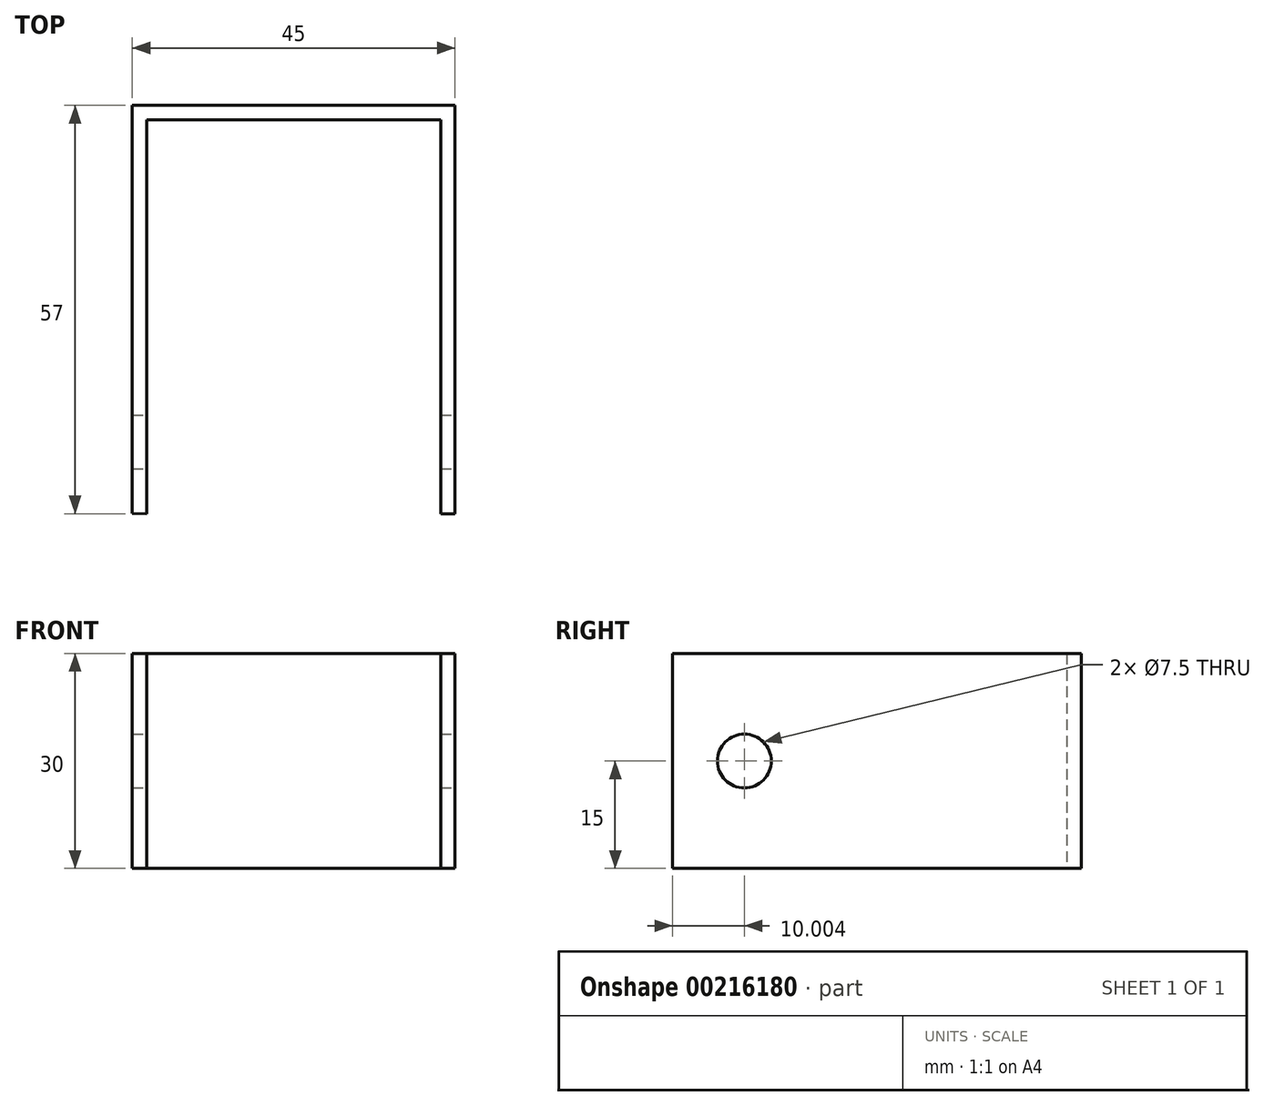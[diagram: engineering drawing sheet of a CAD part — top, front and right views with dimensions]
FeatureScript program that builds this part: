
annotation { "Feature Type Name" : "Feature", "Feature Type Description" : "" }
export const myFeature = defineFeature(function(context is Context, id is Id, definition is map)
    precondition{}
    {
        {
            var Q0;
            Q0=qCreatedBy(makeId("Top.planeOp"),FACE);
            var sketch = newSketch(context, id + "F0", { "sketchPlane" : qUnion([Q0])});
            skLineSegment(sketch, "E0", {"start": v(-24.23, 21.28) * mm, "end": v(16.77, 21.28) * mm});
            skLineSegment(sketch, "E1", {"start": v(-24.23, 21.28) * mm, "end": v(-24.23, -33.72) * mm});
            skLineSegment(sketch, "E2", {"start": v(16.77, 21.28) * mm, "end": v(16.77, -33.72) * mm});
            skLineSegment(sketch, "E3.0", {"start": v(-26.23, 23.28) * mm, "end": v(-26.23, -33.68) * mm});
            skLineSegment(sketch, "E3.1", {"start": v(-26.23, 23.28) * mm, "end": v(18.77, 23.28) * mm});
            skLineSegment(sketch, "E3.2", {"start": v(18.77, 23.28) * mm, "end": v(18.77, -33.72) * mm});
            skLineSegment(sketch, "E4", {"start": v(16.77, -33.72) * mm, "end": v(18.77, -33.72) * mm});
            skLineSegment(sketch, "E5", {"start": v(-24.23, -33.72) * mm, "end": v(-26.23, -33.68) * mm});
            skSolve(sketch);
        }
        {
            var Q0;
            Q0 = qSketchRegion(id + "F0", true);
            extrude(context, id + "F1", {"entities" : qUnion([Q0]), "depth" : 30 * mm});
        }
        {
            var Q0;
            Q0=makeQuery(id+"F1.opExtrude","SWEPT_FACE",FACE,{"disambiguationData":[OSD([sQuery(id+"F0.wireOp",EDGE,"E3.2")])]});
            var sketch = newSketch(context, id + "F2", { "sketchPlane" : qUnion([Q0])});
            skPoint(sketch, "E6", {"position": v(-23.72, 15) * mm});
            skPoint(sketch, "E7", {"position": v(-33.72, 15) * mm});
            skSolve(sketch);
        }
        {
            var Q0;
            Q0=sQuery(id+"F2.wireOp",VERTEX,"E6");
            var Q1;
            Q1=makeQuery(id+"F1.opExtrude","SWEPT_BODY",BODY,{"disambiguationData":[OSD([sQuery(id+"F0.wireOp",EDGE,"E0"),sQuery(id+"F0.wireOp",EDGE,"E1"),sQuery(id+"F0.wireOp",EDGE,"E2"),sQuery(id+"F0.wireOp",EDGE,"E3.0"),sQuery(id+"F0.wireOp",EDGE,"E3.1"),sQuery(id+"F0.wireOp",EDGE,"E3.2"),sQuery(id+"F0.wireOp",EDGE,"E4"),sQuery(id+"F0.wireOp",EDGE,"E5")])]});
            hole(context, id + "F3", {"style" : HoleStyle.SIMPLE, "endStyle" : HoleEndStyle.THROUGH, "holeDiameter" : 7.5 * mm, "locations" : qUnion([Q0]), "scope" : qUnion([Q1]), "isTappedThrough" : true});
        }
    });
